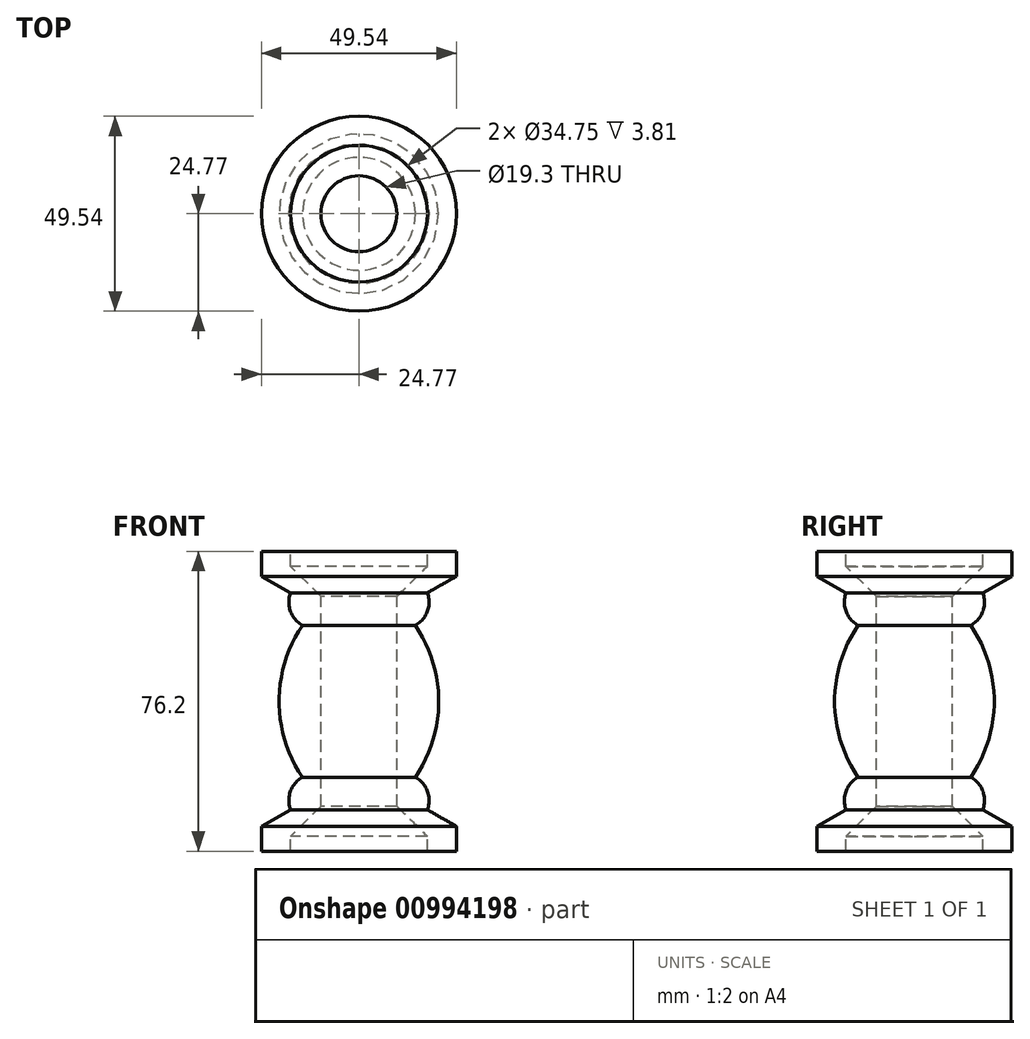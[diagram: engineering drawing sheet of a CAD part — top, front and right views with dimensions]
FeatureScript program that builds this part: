
annotation { "Feature Type Name" : "Feature", "Feature Type Description" : "" }
export const myFeature = defineFeature(function(context is Context, id is Id, definition is map)
    precondition{}
    {
        {
            var Q0;
            Q0=qCreatedBy(makeId("Front.planeOp"),FACE);
            var sketch = newSketch(context, id + "F0", { "sketchPlane" : qUnion([Q0])});
            skLineSegment(sketch, "E0", {"start": v(0, 61.77) * mm, "end": v(0, -61.77) * mm, "construction": true});
            skLineSegment(sketch, "E1", {"start": v(-24.77, 0) * mm, "end": v(-24.77, -6.35) * mm, "construction": true});
            skPoint(sketch, "E1.endSnap0", {"position": v(-24.77, 0) * mm});
            skPoint(sketch, "E1.endSnap1", {"position": v(-32.87, -6.35) * mm});
            skLineSegment(sketch, "E2", {"start": v(-24.77, -6.35) * mm, "end": v(-17.37, -10.54) * mm, "construction": true});
            skLineSegment(sketch, "E3", {"start": v(-17.37, -10.54) * mm, "end": v(-21.07, -8.45) * mm, "construction": true});
            skLineSegment(sketch, "E4", {"start": v(-24.77, 0) * mm, "end": v(-24.77, -6.35) * mm});
            skLineSegment(sketch, "E5", {"start": v(-24.77, -6.35) * mm, "end": v(-17.37, -10.54) * mm});
            skArc(sketch, "E6", {"start": v(-17.37, -10.54) * mm, "mid": v(-17.4, -15.25) * mm, "end": v(-14.33, -18.82) * mm});
            skArc(sketch, "E7", {"start": v(-14.33, -18.82) * mm, "mid": v(-20.27, -38.1) * mm, "end": v(-14.33, -57.38) * mm});
            skLineSegment(sketch, "E8", {"start": v(-52.85, -38.1) * mm, "end": v(77.55, -38.1) * mm});
            skLineSegment(sketch, "E9", {"start": v(-24.77, 0) * mm, "end": v(-17.37, 0) * mm});
            skLineSegment(sketch, "E10", {"start": v(-17.37, 0) * mm, "end": v(-17.37, -3.8) * mm});
            skLineSegment(sketch, "E11", {"start": v(-17.37, -3.8) * mm, "end": v(-9.65, -11.43) * mm});
            skLineSegment(sketch, "E12", {"start": v(-9.65, -11.43) * mm, "end": v(-9.65, -38.1) * mm});
            skLineSegment(sketch, "E13.MirrorCS", {"start": v(-24.77, -76.2) * mm, "end": v(-17.37, -76.2) * mm});
            skLineSegment(sketch, "E14.MirrorCS", {"start": v(-24.77, -76.2) * mm, "end": v(-24.77, -69.85) * mm, "construction": true});
            skLineSegment(sketch, "E15.MirrorCS", {"start": v(-24.77, -69.85) * mm, "end": v(-17.37, -65.66) * mm, "construction": true});
            skLineSegment(sketch, "E16.MirrorCS", {"start": v(-17.37, -72.39) * mm, "end": v(-9.65, -64.77) * mm});
            skArc(sketch, "E17.MirrorCS", {"start": v(-17.37, -65.66) * mm, "mid": v(-17.4, -60.95) * mm, "end": v(-14.33, -57.38) * mm});
            skLineSegment(sketch, "E18.MirrorCS", {"start": v(-9.65, -64.77) * mm, "end": v(-9.65, -38.1) * mm});
            skLineSegment(sketch, "E19", {"start": v(-17.37, -76.2) * mm, "end": v(-17.37, -72.39) * mm});
            skLineSegment(sketch, "E20", {"start": v(-24.77, -69.85) * mm, "end": v(-17.37, -65.66) * mm});
            skLineSegment(sketch, "E21", {"start": v(-24.77, -69.85) * mm, "end": v(-24.77, -76.2) * mm});
            skSolve(sketch);
        }
        {
            var Q0;
            Q0=makeQuery(id+"F0.imprint","IMPRINT",FACE,{"disambiguationData":[TD([[makeQuery(id+"F0.imprint","IMPRINT",EDGE,{"derivedFrom":sQuery(id+"F0.wireOp",EDGE,"E4")}),1.0]])]});
            var Q1;
            Q1=makeQuery(id+"F0.imprint","IMPRINT",FACE,{"disambiguationData":[TD([[makeQuery(id+"F0.imprint","IMPRINT",EDGE,{"derivedFrom":sQuery(id+"F0.wireOp",EDGE,"E13.MirrorCS")}),1.0]])]});
            var Q2;
            Q2=sQuery(id+"F0.wireOp",EDGE,"E0");
            revolve(context, id + "F1", {"surfaceOperationType" : NewSurfaceOperationType.NEW, "entities" : qUnion([Q0, Q1]), "axis" : qUnion([Q2]), "revolveType" : RevolveType.FULL});
        }
    });
